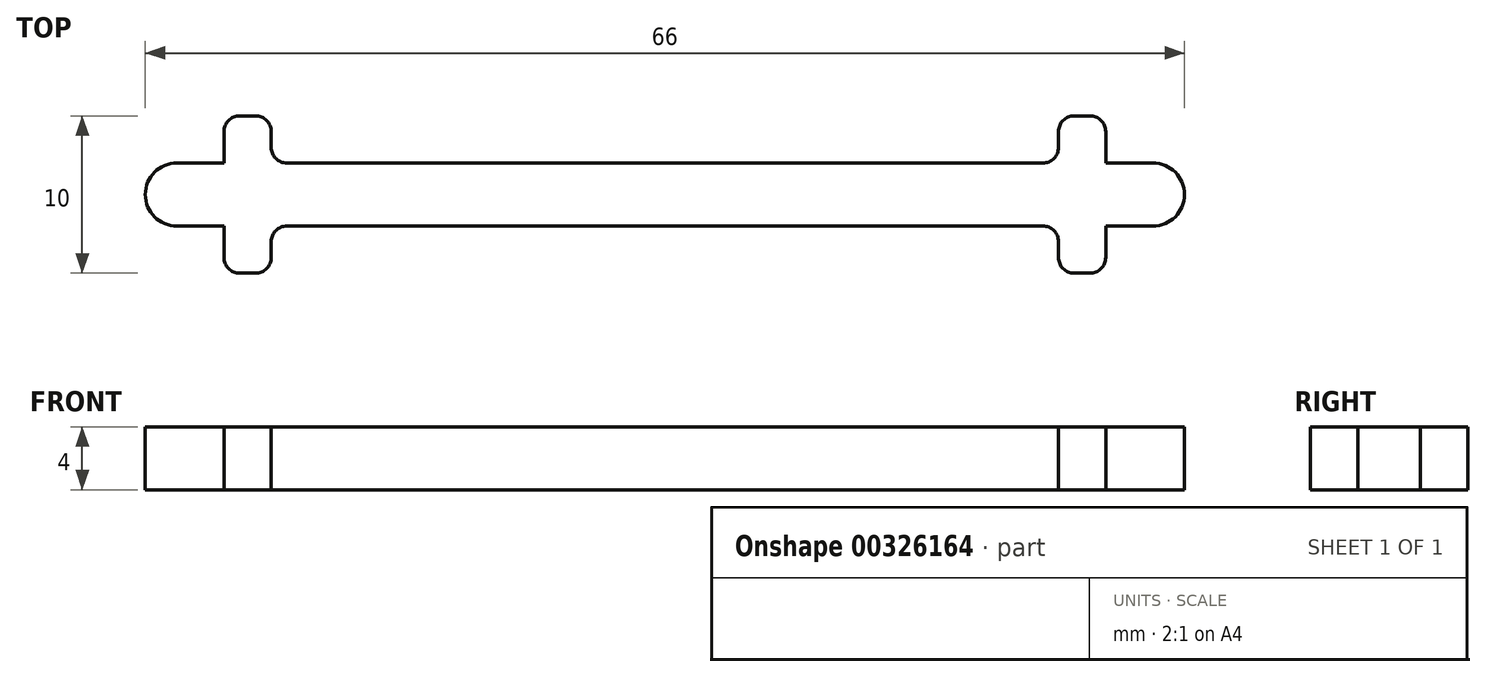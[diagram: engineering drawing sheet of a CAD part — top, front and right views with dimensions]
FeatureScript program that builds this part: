
annotation { "Feature Type Name" : "Feature", "Feature Type Description" : "" }
export const myFeature = defineFeature(function(context is Context, id is Id, definition is map)
    precondition{}
    {
        {
            var Q0;
            Q0=qCreatedBy(makeId("Top.planeOp"),FACE);
            var sketch = newSketch(context, id + "F0", { "sketchPlane" : qUnion([Q0])});
            skLineSegment(sketch, "E0.bottom", {"start": v(-33, 2) * mm, "end": v(-28, 2) * mm});
            skLineSegment(sketch, "E0.top", {"start": v(-33, -2) * mm, "end": v(-28, -2) * mm});
            skLineSegment(sketch, "E0.left", {"start": v(-33, 2) * mm, "end": v(-33, -2) * mm});
            skLineSegment(sketch, "E0.right", {"start": v(33, 2) * mm, "end": v(33, -2) * mm});
            skPoint(sketch, "E0.middle", {"position": v(0, 0) * mm});
            skLineSegment(sketch, "E1", {"start": v(-28, 2) * mm, "end": v(-28, 5) * mm});
            skLineSegment(sketch, "E2", {"start": v(-28, 5) * mm, "end": v(-25, 5) * mm});
            skLineSegment(sketch, "E3", {"start": v(-25, 5) * mm, "end": v(-25, 2) * mm});
            skLineSegment(sketch, "E4.trimOffspring", {"start": v(-25, 2) * mm, "end": v(25, 2) * mm});
            skLineSegment(sketch, "E5", {"start": v(0, 0) * mm, "end": v(-33, 0) * mm, "construction": true});
            skLineSegment(sketch, "E6.MirrorCS", {"start": v(-25, -5) * mm, "end": v(-25, -2) * mm});
            skLineSegment(sketch, "E7.MirrorCS", {"start": v(-28, -5) * mm, "end": v(-25, -5) * mm});
            skLineSegment(sketch, "E8.MirrorCS", {"start": v(-28, -2) * mm, "end": v(-28, -5) * mm});
            skLineSegment(sketch, "E9.trimOffspring", {"start": v(-25, -2) * mm, "end": v(25, -2) * mm});
            skLineSegment(sketch, "E10", {"start": v(0, 0) * mm, "end": v(0, 13.68) * mm, "construction": true});
            skLineSegment(sketch, "E11.MirrorCS", {"start": v(28, -2) * mm, "end": v(28, -5) * mm});
            skLineSegment(sketch, "E12.MirrorCS", {"start": v(28, 2) * mm, "end": v(28, 5) * mm});
            skLineSegment(sketch, "E13.MirrorCS", {"start": v(28, 5) * mm, "end": v(25, 5) * mm});
            skLineSegment(sketch, "E14.MirrorCS", {"start": v(25, 5) * mm, "end": v(25, 2) * mm});
            skLineSegment(sketch, "E15.MirrorCS", {"start": v(28, -5) * mm, "end": v(25, -5) * mm});
            skLineSegment(sketch, "E16.MirrorCS", {"start": v(25, -5) * mm, "end": v(25, -2) * mm});
            skLineSegment(sketch, "E17.trimOffspring", {"start": v(28, 2) * mm, "end": v(33, 2) * mm});
            skLineSegment(sketch, "E18.trimOffspring", {"start": v(28, -2) * mm, "end": v(33, -2) * mm});
            skSolve(sketch);
        }
        {
            var Q0;
            Q0 = qSketchRegion(id + "F0", true);
            extrude(context, id + "F1", {"entities" : qUnion([Q0]), "depth" : 4 * mm});
        }
        {
            var Q0;
            Q0=makeQuery(id+"F1.opExtrude","SWEPT_EDGE",EDGE,{"disambiguationData":[OSD([sQuery(id+"F0.wireOp",EDGE,"E0.right"),sQuery(id+"F0.wireOp",EDGE,"E18.trimOffspring")])]});
            var Q1;
            Q1=makeQuery(id+"F1.opExtrude","SWEPT_EDGE",EDGE,{"disambiguationData":[OSD([sQuery(id+"F0.wireOp",EDGE,"E0.right"),sQuery(id+"F0.wireOp",EDGE,"E17.trimOffspring")])]});
            var Q2;
            Q2=makeQuery(id+"F1.opExtrude","SWEPT_EDGE",EDGE,{"disambiguationData":[OSD([sQuery(id+"F0.wireOp",EDGE,"E0.top"),sQuery(id+"F0.wireOp",EDGE,"E0.left")])]});
            var Q3;
            Q3=makeQuery(id+"F1.opExtrude","SWEPT_EDGE",EDGE,{"disambiguationData":[OSD([sQuery(id+"F0.wireOp",EDGE,"E0.bottom"),sQuery(id+"F0.wireOp",EDGE,"E0.left")])]});
            fillet(context, id + "F2", {"entities" : qUnion([Q0, Q1, Q2, Q3]), "radius" : 2 * mm, "tangentPropagation" : true, "allowEdgeOverflow" : false});
        }
        {
            var Q0;
            Q0=makeQuery(id+"F1.opExtrude","SWEPT_EDGE",EDGE,{"disambiguationData":[OSD([sQuery(id+"F0.wireOp",EDGE,"E7.MirrorCS"),sQuery(id+"F0.wireOp",EDGE,"E8.MirrorCS")])]});
            var Q1;
            Q1=makeQuery(id+"F1.opExtrude","SWEPT_EDGE",EDGE,{"disambiguationData":[OSD([sQuery(id+"F0.wireOp",EDGE,"E1"),sQuery(id+"F0.wireOp",EDGE,"E2")])]});
            var Q2;
            Q2=makeQuery(id+"F1.opExtrude","SWEPT_EDGE",EDGE,{"disambiguationData":[OSD([sQuery(id+"F0.wireOp",EDGE,"E11.MirrorCS"),sQuery(id+"F0.wireOp",EDGE,"E15.MirrorCS")])]});
            var Q3;
            Q3=makeQuery(id+"F1.opExtrude","SWEPT_EDGE",EDGE,{"disambiguationData":[OSD([sQuery(id+"F0.wireOp",EDGE,"E12.MirrorCS"),sQuery(id+"F0.wireOp",EDGE,"E13.MirrorCS")])]});
            var Q4;
            Q4=makeQuery(id+"F1.opExtrude","SWEPT_EDGE",EDGE,{"disambiguationData":[OSD([sQuery(id+"F0.wireOp",EDGE,"E6.MirrorCS"),sQuery(id+"F0.wireOp",EDGE,"E7.MirrorCS")])]});
            var Q5;
            Q5=makeQuery(id+"F1.opExtrude","SWEPT_EDGE",EDGE,{"disambiguationData":[OSD([sQuery(id+"F0.wireOp",EDGE,"E2"),sQuery(id+"F0.wireOp",EDGE,"E3")])]});
            var Q6;
            Q6=makeQuery(id+"F1.opExtrude","SWEPT_EDGE",EDGE,{"disambiguationData":[OSD([sQuery(id+"F0.wireOp",EDGE,"E13.MirrorCS"),sQuery(id+"F0.wireOp",EDGE,"E14.MirrorCS")])]});
            var Q7;
            Q7=makeQuery(id+"F1.opExtrude","SWEPT_EDGE",EDGE,{"disambiguationData":[OSD([sQuery(id+"F0.wireOp",EDGE,"E15.MirrorCS"),sQuery(id+"F0.wireOp",EDGE,"E16.MirrorCS")])]});
            var Q8;
            Q8=makeQuery(id+"F1.opExtrude","SWEPT_EDGE",EDGE,{"disambiguationData":[OSD([sQuery(id+"F0.wireOp",EDGE,"E9.trimOffspring"),sQuery(id+"F0.wireOp",EDGE,"E16.MirrorCS")])]});
            var Q9;
            Q9=makeQuery(id+"F1.opExtrude","SWEPT_EDGE",EDGE,{"disambiguationData":[OSD([sQuery(id+"F0.wireOp",EDGE,"E4.trimOffspring"),sQuery(id+"F0.wireOp",EDGE,"E14.MirrorCS")])]});
            var Q10;
            Q10=makeQuery(id+"F1.opExtrude","SWEPT_EDGE",EDGE,{"disambiguationData":[OSD([sQuery(id+"F0.wireOp",EDGE,"E3"),sQuery(id+"F0.wireOp",EDGE,"E4.trimOffspring")])]});
            var Q11;
            Q11=makeQuery(id+"F1.opExtrude","SWEPT_EDGE",EDGE,{"disambiguationData":[OSD([sQuery(id+"F0.wireOp",EDGE,"E6.MirrorCS"),sQuery(id+"F0.wireOp",EDGE,"E9.trimOffspring")])]});
            fillet(context, id + "F3", {"entities" : qUnion([Q0, Q1, Q2, Q3, Q4, Q5, Q6, Q7, Q8, Q9, Q10, Q11]), "radius" : 1 * mm, "tangentPropagation" : true, "allowEdgeOverflow" : false});
        }
    });
